# Revit family: TR-036_RFA
name_source: partatom
category: Aparatos sanitarios
units: mm (PartAtom-declared; Revit-internal decimal feet)

## family parameters
Compartido = No
Corte con vacíos al cargar = No
Cota de conector redondo = Diámetro de uso
Número OmniClass = 23.45.00.00
Punto de cálculo de habitación = No
Se basa en plano de trabajo = No
Siempre vertical = Sí
Tipo de pieza = Normal
Título OmniClass = Sanitary, Laundry, and Cleaning Equipment

## types (1)
- TR-036
    Brass Chromed = Brass
    Comentarios de tipo = Arms And Escutcheons For Showerheads
    Data Sheet = http://helvex.com
    Descripción = Kúbica Wall Mounted Arm And Escutcheon
    Elevación por defecto = 0"
    Fabricante = HELVEX
    Features = Sliding Escutcheon; Wall Arm
    Instructive = http://helvex.com
    Modelo = TR-036
    Niquel Duravex = Niquel Duravex
    Satin = Satin
    Support Base Diameter = 2"
    Total Length = 17"
    URL = http://helvex.com

## geometry (parser evidence)
native form markers: Sweep x2
no freeform markers — native parametric forms only
